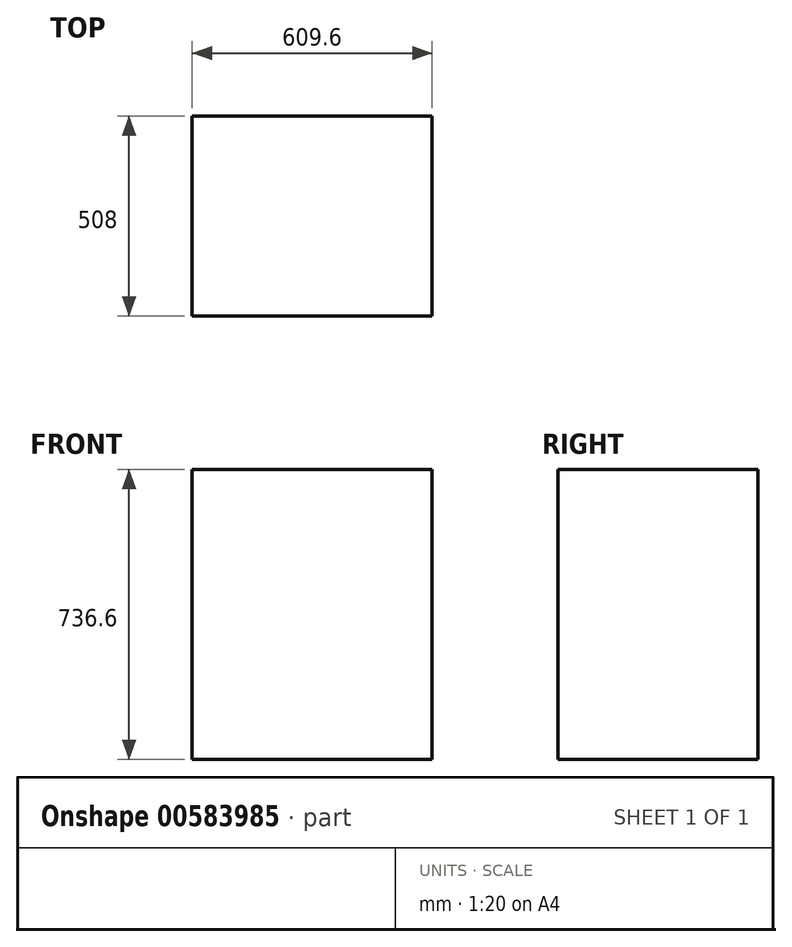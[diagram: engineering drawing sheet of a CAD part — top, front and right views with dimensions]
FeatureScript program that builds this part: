
annotation { "Feature Type Name" : "Feature", "Feature Type Description" : "" }
export const myFeature = defineFeature(function(context is Context, id is Id, definition is map)
    precondition{}
    {
        {
            var Q0;
            Q0=qCreatedBy(makeId("Top.planeOp"),FACE);
            var sketch = newSketch(context, id + "F0", { "sketchPlane" : qUnion([Q0])});
            skLineSegment(sketch, "E0.bottom", {"start": v(-469.4, 246.2) * mm, "end": v(140.2, 246.2) * mm});
            skLineSegment(sketch, "E0.top", {"start": v(-469.4, -261.8) * mm, "end": v(140.2, -261.8) * mm});
            skLineSegment(sketch, "E0.left", {"start": v(-469.4, 246.2) * mm, "end": v(-469.4, -261.8) * mm});
            skLineSegment(sketch, "E0.right", {"start": v(140.2, 246.2) * mm, "end": v(140.2, -261.8) * mm});
            skSolve(sketch);
        }
        {
            var Q0;
            Q0=makeQuery(id+"F0.imprint","IMPRINT",FACE,{"disambiguationData":[TD([[makeQuery(id+"F0.imprint","IMPRINT",EDGE,{"derivedFrom":sQuery(id+"F0.wireOp",EDGE,"E0.bottom")}),-1.0]])]});
            extrude(context, id + "F1", {"entities" : qUnion([Q0]), "depth" : 736.6 * mm, "offsetDistance" : 25.4 * mm});
        }
    });
